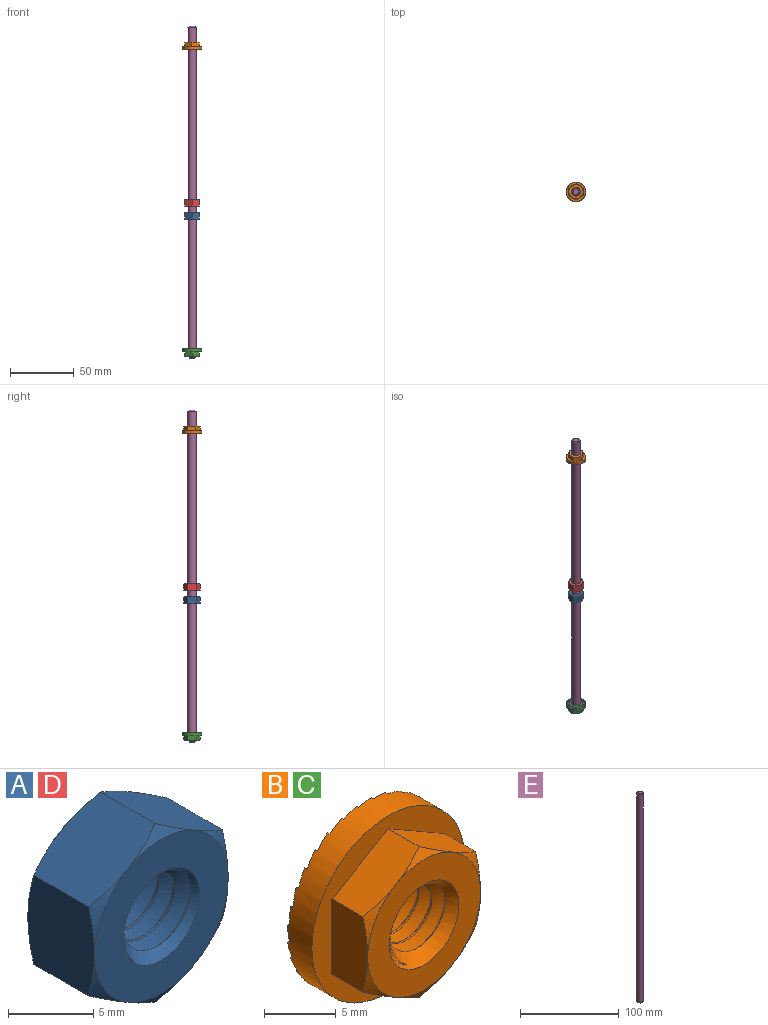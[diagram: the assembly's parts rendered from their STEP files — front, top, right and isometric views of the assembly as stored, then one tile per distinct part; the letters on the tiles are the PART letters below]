
ASSEMBLY  parts=5 mates=4
PART A: 26 faces, bbox 13.4x7x13.4 mm
  f0: cone r=2.86mm half-angle=45deg, axis (0,1,0), area 10.5mm2, adj f10,f11,f12,f13
  f1: cone r=2.86mm half-angle=45deg, axis (0,-1,0), area 10.5mm2, adj f3,f11,f12,f13
  f2: cylinder r=3.17mm len=6.35mm, axis (0,1,0), area 13.9mm2, adj f3,f10,f11,f13
  f3: plane 11.11x11.11mm, normal (0,-1,0), area 65.3mm2, adj f1,f2,f14,f15,f16,f17,f18,f19
  f4: plane 6.08x6.08mm, normal (-0.5,0,0.87), area 33.5mm2, adj f5,f9,f14,f19,f21,f22
  f5: plane 6.95x6.09mm, normal (-1,0,0), area 33.5mm2, adj f4,f6,f18,f19,f22,f23
  f6: plane 6.08x6.08mm, normal (-0.5,0,-0.87), area 33.5mm2, adj f5,f7,f17,f18,f23,f24
  f7: plane 6.08x6.08mm, normal (0.5,0,-0.87), area 33.5mm2, adj f6,f8,f16,f17,f24,f25
  f8: plane 6.95x6.09mm, normal (1,0,0), area 33.5mm2, adj f7,f9,f15,f16,f20,f25
  f9: plane 6.08x6.08mm, normal (0.5,0,0.87), area 33.5mm2, adj f4,f8,f14,f15,f20,f21
  f10: plane 11.11x11.11mm, normal (0,1,0), area 65.3mm2, adj f0,f2,f20,f21,f22,f23,f24,f25
  f11: bspline ~6.35x6.35mm, area 59.4mm2, adj f0,f1,f2,f12
  f12: cylinder r=2.35mm len=4.7mm, axis (0,-1,0), area 7.2mm2, adj f0,f1,f11,f13
  f13: bspline ~6.35x6.35mm, area 62.2mm2, adj f0,f1,f2,f12
  f14: cone r=5.56mm half-angle=60deg, axis (0,1,0), area 3mm2, adj f3,f4,f9
  f15: cone r=5.56mm half-angle=60deg, axis (0,1,0), area 3mm2, adj f3,f8,f9
  f16: cone r=5.56mm half-angle=60deg, axis (0,1,0), area 3mm2, adj f3,f7,f8
  f17: cone r=5.56mm half-angle=60deg, axis (0,1,0), area 3mm2, adj f3,f6,f7
  f18: cone r=5.56mm half-angle=60deg, axis (0,1,0), area 3mm2, adj f3,f5,f6
  f19: cone r=5.56mm half-angle=60deg, axis (0,1,0), area 3mm2, adj f3,f4,f5
  f20: cone r=5.56mm half-angle=60deg, axis (0,-1,0), area 3mm2, adj f8,f9,f10
  f21: cone r=5.56mm half-angle=60deg, axis (0,-1,0), area 3mm2, adj f4,f9,f10
  f22: cone r=5.56mm half-angle=60deg, axis (0,-1,0), area 3mm2, adj f4,f5,f10
  f23: cone r=5.56mm half-angle=60deg, axis (0,-1,0), area 3mm2, adj f5,f6,f10
  f24: cone r=5.56mm half-angle=60deg, axis (0,-1,0), area 3mm2, adj f6,f7,f10
  f25: cone r=5.56mm half-angle=60deg, axis (0,-1,0), area 3mm2, adj f7,f8,f10
PART B: 88 faces, bbox 15.6x7.1x15.6 mm
  f0: cone r=3.43mm half-angle=45deg, axis (0,1,0), area 17.9mm2, adj f1,f3,f4,f7,f22,f23
  f1: cone r=3.43mm half-angle=45deg, axis (0,1,0), area 0mm2, adj f0,f4,f22
  f2: cone r=3.43mm half-angle=45deg, axis (0,-1,0), area 18mm2, adj f3,f4,f21,f22,f23
  f3: cylinder r=3.17mm len=6.35mm, axis (0,1,0), area 13.6mm2, adj f0,f2,f22,f23
  f4: cylinder r=2.35mm len=4.7mm, axis (0,-1,0), area 7mm2, adj f0,f1,f2,f22,f23
  f5: cylinder r=7.54mm len=15.08mm, axis (0,1,0), area 109.8mm2, adj f14,f24,f25,f26,f27,f28,f29,f30
  f6: cylinder r=5.46mm len=10.92mm, axis (0,1,0), area 4.2mm2, adj f7,f24,f25,f26,f27,f28,f29,f30
  f7: plane 10.92x10.92mm, normal (0,1,0), area 56.8mm2, adj f0,f6
  f8: plane 6.08x4.04mm, normal (0.5,0,0.87), area 21.5mm2, adj f9,f13,f14,f19,f20
  f9: plane 6.95x4.04mm, normal (1,0,0), area 21.5mm2, adj f8,f10,f14,f15,f20
  f10: plane 6.08x4.04mm, normal (0.5,0,-0.87), area 21.5mm2, adj f9,f11,f14,f15,f16
  f11: plane 6.08x4.04mm, normal (-0.5,0,-0.87), area 21.5mm2, adj f10,f12,f14,f16,f17
  f12: plane 6.95x4.04mm, normal (-1,0,0), area 21.5mm2, adj f11,f13,f14,f17,f18
  f13: plane 6.08x4.04mm, normal (-0.5,0,0.87), area 21.5mm2, adj f8,f12,f14,f18,f19
  f14: plane 15.08x15.08mm, normal (0,-1,0), area 71.7mm2, adj f5,f8,f9,f10,f11,f12,f13
  f15: cone r=5.56mm half-angle=60deg, axis (0,1,0), area 3mm2, adj f9,f10,f21
  f16: cone r=5.56mm half-angle=60deg, axis (0,1,0), area 3mm2, adj f10,f11,f21
  f17: cone r=5.56mm half-angle=60deg, axis (0,1,0), area 3mm2, adj f11,f12,f21
  f18: cone r=5.56mm half-angle=60deg, axis (0,1,0), area 3mm2, adj f12,f13,f21
  f19: cone r=5.56mm half-angle=60deg, axis (0,1,0), area 3mm2, adj f8,f13,f21
  f20: cone r=5.56mm half-angle=60deg, axis (0,1,0), area 3mm2, adj f8,f9,f21
  f21: plane 11.11x11.11mm, normal (0,-1,0), area 60mm2, adj f2,f15,f16,f17,f18,f19,f20
  f22: bspline ~7.33x6.35mm, area 60.8mm2, adj f0,f1,f2,f3,f4
  f23: bspline ~7.33x6.35mm, area 62.2mm2, adj f0,f2,f3,f4
  f24: plane 2.07x0.24mm, normal (1,0,-0.1), area 0.4mm2, adj f5,f6,f25,f87
  f25: plane 2.11x1.48mm, normal (-0.16,0.99,0), area 2.7mm2, adj f5,f6,f24,f26
  f26: plane 2.07x0.24mm, normal (1,0,0.1), area 0.4mm2, adj f5,f6,f25,f27
  f27: plane 2.28x1.65mm, normal (-0.16,0.99,-0.03), area 2.7mm2, adj f5,f6,f26,f28
  f28: plane 1.99x0.6mm, normal (0.96,0,0.29), area 0.4mm2, adj f5,f6,f27,f29
  f29: plane 2.4x1.97mm, normal (-0.15,0.99,-0.06), area 2.7mm2, adj f5,f6,f28,f30
  f30: plane 1.83x0.98mm, normal (0.88,0,0.47), area 0.4mm2, adj f5,f6,f29,f31
  f31: plane 2.43x2.21mm, normal (-0.14,0.99,-0.09), area 2.7mm2, adj f5,f6,f30,f32
  f32: plane 1.61x1.32mm, normal (0.77,0,0.63), area 0.4mm2, adj f5,f6,f31,f33
  f33: plane 2.36x2.36mm, normal (-0.12,0.99,-0.12), area 2.7mm2, adj f5,f6,f32,f34
  f34: plane 1.61x1.32mm, normal (0.63,0,0.77), area 0.4mm2, adj f5,f6,f33,f35
  f35: plane 2.43x2.21mm, normal (-0.09,0.99,-0.14), area 2.7mm2, adj f5,f6,f34,f36
  f36: plane 1.83x0.98mm, normal (0.47,0,0.88), area 0.4mm2, adj f5,f6,f35,f37
  f37: plane 2.4x1.97mm, normal (-0.06,0.99,-0.15), area 2.7mm2, adj f5,f6,f36,f38
  f38: plane 1.99x0.6mm, normal (0.29,0,0.96), area 0.4mm2, adj f5,f6,f37,f39
  f39: plane 2.28x1.65mm, normal (-0.03,0.99,-0.16), area 2.7mm2, adj f5,f6,f38,f40
  f40: plane 2.07x0.24mm, normal (0.1,0,1), area 0.4mm2, adj f5,f6,f39,f41
  f41: plane 2.11x1.48mm, normal (0,0.99,-0.16), area 2.7mm2, adj f5,f6,f40,f42
  f42: plane 2.07x0.24mm, normal (-0.1,0,1), area 0.4mm2, adj f5,f6,f41,f43
  f43: plane 2.28x1.65mm, normal (0.03,0.99,-0.16), area 2.7mm2, adj f5,f6,f42,f44
  f44: plane 1.99x0.6mm, normal (-0.29,0,0.96), area 0.4mm2, adj f5,f6,f43,f45
  f45: plane 2.4x1.97mm, normal (0.06,0.99,-0.15), area 2.7mm2, adj f5,f6,f44,f46
  f46: plane 1.83x0.98mm, normal (-0.47,0,0.88), area 0.4mm2, adj f5,f6,f45,f47
  f47: plane 2.43x2.21mm, normal (0.09,0.99,-0.14), area 2.7mm2, adj f5,f6,f46,f48
  f48: plane 1.61x1.32mm, normal (-0.63,0,0.77), area 0.4mm2, adj f5,f6,f47,f49
  f49: plane 2.36x2.36mm, normal (0.12,0.99,-0.12), area 2.7mm2, adj f5,f6,f48,f50
  f50: plane 1.61x1.32mm, normal (-0.77,0,0.63), area 0.4mm2, adj f5,f6,f49,f51
  f51: plane 2.43x2.21mm, normal (0.14,0.99,-0.09), area 2.7mm2, adj f5,f6,f50,f52
  f52: plane 1.83x0.98mm, normal (-0.88,0,0.47), area 0.4mm2, adj f5,f6,f51,f53
  f53: plane 2.4x1.97mm, normal (0.15,0.99,-0.06), area 2.7mm2, adj f5,f6,f52,f54
  f54: plane 1.99x0.6mm, normal (-0.96,0,0.29), area 0.4mm2, adj f5,f6,f53,f55
  f55: plane 2.28x1.65mm, normal (0.16,0.99,-0.03), area 2.7mm2, adj f5,f6,f54,f56
  f56: plane 2.07x0.24mm, normal (-1,0,0.1), area 0.4mm2, adj f5,f6,f55,f57
  f57: plane 2.11x1.48mm, normal (0.16,0.99,0), area 2.7mm2, adj f5,f6,f56,f58
  f58: plane 2.07x0.24mm, normal (-1,0,-0.1), area 0.4mm2, adj f5,f6,f57,f59
  f59: plane 2.28x1.65mm, normal (0.16,0.99,0.03), area 2.7mm2, adj f5,f6,f58,f60
  f60: plane 1.99x0.6mm, normal (-0.96,0,-0.29), area 0.4mm2, adj f5,f6,f59,f61
  f61: plane 2.4x1.97mm, normal (0.15,0.99,0.06), area 2.7mm2, adj f5,f6,f60,f62
  f62: plane 1.83x0.98mm, normal (-0.88,0,-0.47), area 0.4mm2, adj f5,f6,f61,f63
  f63: plane 2.43x2.21mm, normal (0.14,0.99,0.09), area 2.7mm2, adj f5,f6,f62,f64
  f64: plane 1.61x1.32mm, normal (-0.77,0,-0.63), area 0.4mm2, adj f5,f6,f63,f65
  f65: plane 2.36x2.36mm, normal (0.12,0.99,0.12), area 2.7mm2, adj f5,f6,f64,f66
  f66: plane 1.61x1.32mm, normal (-0.63,0,-0.77), area 0.4mm2, adj f5,f6,f65,f67
  f67: plane 2.43x2.21mm, normal (0.09,0.99,0.14), area 2.7mm2, adj f5,f6,f66,f68
  f68: plane 1.83x0.98mm, normal (-0.47,0,-0.88), area 0.4mm2, adj f5,f6,f67,f69
  f69: plane 2.4x1.97mm, normal (0.06,0.99,0.15), area 2.7mm2, adj f5,f6,f68,f70
  f70: plane 1.99x0.6mm, normal (-0.29,0,-0.96), area 0.4mm2, adj f5,f6,f69,f71
  f71: plane 2.28x1.65mm, normal (0.03,0.99,0.16), area 2.7mm2, adj f5,f6,f70,f72
  f72: plane 2.07x0.24mm, normal (-0.1,0,-1), area 0.4mm2, adj f5,f6,f71,f73
  f73: plane 2.11x1.48mm, normal (0,0.99,0.16), area 2.7mm2, adj f5,f6,f72,f74
  f74: plane 2.07x0.24mm, normal (0.1,0,-1), area 0.4mm2, adj f5,f6,f73,f75
  f75: plane 2.28x1.65mm, normal (-0.03,0.99,0.16), area 2.7mm2, adj f5,f6,f74,f76
  f76: plane 1.99x0.6mm, normal (0.29,0,-0.96), area 0.4mm2, adj f5,f6,f75,f77
  f77: plane 2.4x1.97mm, normal (-0.06,0.99,0.15), area 2.7mm2, adj f5,f6,f76,f78
  f78: plane 1.83x0.98mm, normal (0.47,0,-0.88), area 0.4mm2, adj f5,f6,f77,f79
  f79: plane 2.43x2.21mm, normal (-0.09,0.99,0.14), area 2.7mm2, adj f5,f6,f78,f80
  f80: plane 1.61x1.32mm, normal (0.63,0,-0.77), area 0.4mm2, adj f5,f6,f79,f81
  f81: plane 2.36x2.36mm, normal (-0.12,0.99,0.12), area 2.7mm2, adj f5,f6,f80,f82
  f82: plane 1.61x1.32mm, normal (0.77,0,-0.63), area 0.4mm2, adj f5,f6,f81,f83
  f83: plane 2.43x2.21mm, normal (-0.14,0.99,0.09), area 2.7mm2, adj f5,f6,f82,f84
  f84: plane 1.83x0.98mm, normal (0.88,0,-0.47), area 0.4mm2, adj f5,f6,f83,f85
  f85: plane 2.4x1.97mm, normal (-0.15,0.99,0.06), area 2.7mm2, adj f5,f6,f84,f86
  f86: plane 1.99x0.6mm, normal (0.96,0,-0.29), area 0.4mm2, adj f5,f6,f85,f87
  f87: plane 2.28x1.65mm, normal (-0.16,0.99,0.03), area 2.7mm2, adj f5,f6,f24,f86
PART C: same geometry as B
PART D: same geometry as A
PART E: 5 faces, bbox 6.4x6.4x260.4 mm
  f0: cylinder r=3.17mm len=258.57mm, axis (0,0,-1), area 5158.3mm2, adj f3,f4
  f1: plane 4.57x4.57mm, normal (0,0,1), area 16.4mm2, adj f3
  f2: plane 4.57x4.57mm, normal (0,0,-1), area 16.4mm2, adj f4
  f3: cone r=2.29mm half-angle=45deg, axis (0,0,-1), area 21.6mm2, adj f0,f1
  f4: cone r=3.17mm half-angle=45deg, axis (0,0,1), area 21.6mm2, adj f0,f2
PLACE A rot(axis=(1,0,0),90deg) t=(-30.32,23.24,26.35)mm
PLACE B rot(axis=(-1,0.01,-0.01),90deg) t=(-30.32,23.24,162.91)mm
PLACE C rot(axis=(0,0.71,0.71),180deg) t=(-30.32,23.24,-83.38)mm
PLACE D rot(axis=(1,0,0),90deg) t=(-30.32,23.24,36.67)mm
PLACE E t=(-30.32,9.86,-84.73)mm
MATE cylindrical B.f0 <-> E.f0  axis (0,0,1) through (-30.32,23.24,159.94)mm
MATE cylindrical C.f0 <-> E.f0  axis (0,0,1) through (-30.32,23.24,-78.64)mm
MATE cylindrical D.f12 <-> E.f0  axis (0,0,-1) through (-30.32,23.24,36.67)mm
MATE cylindrical A.f12 <-> E.f0  axis (0,0,-1) through (-30.32,23.24,26.35)mm
